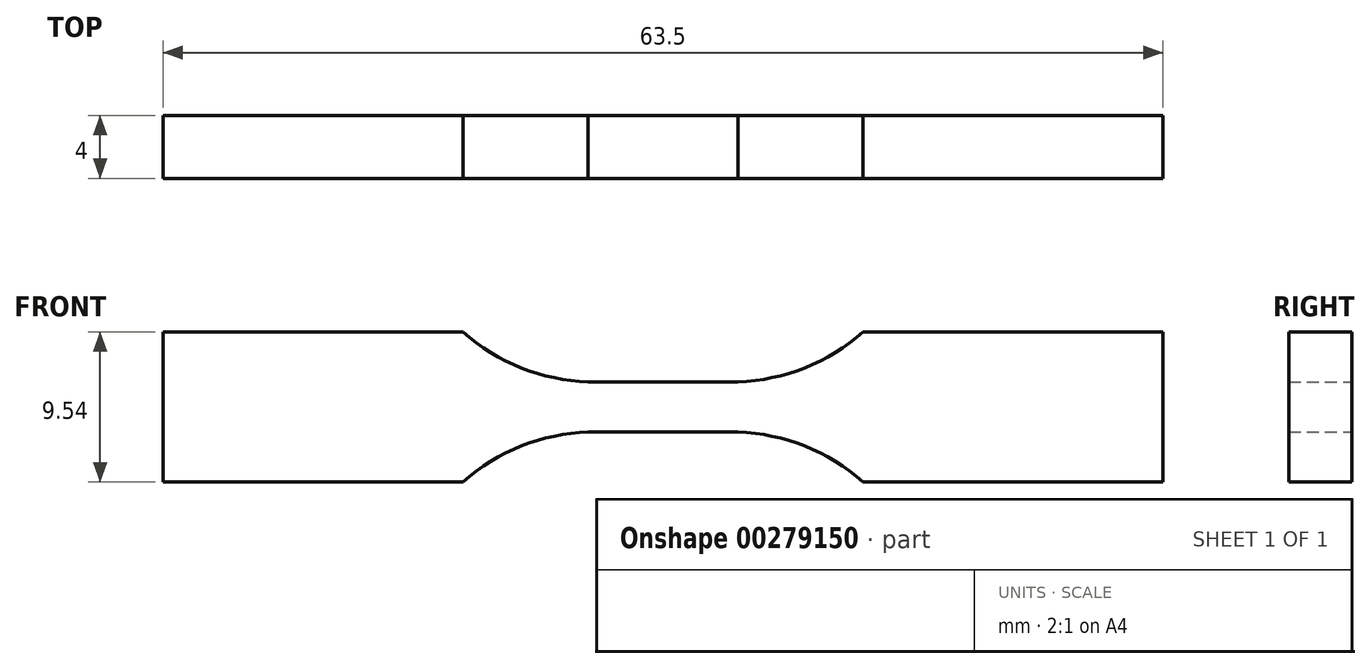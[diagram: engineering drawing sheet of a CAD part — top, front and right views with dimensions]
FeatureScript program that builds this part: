
annotation { "Feature Type Name" : "Feature", "Feature Type Description" : "" }
export const myFeature = defineFeature(function(context is Context, id is Id, definition is map)
    precondition{}
    {
        {
            var Q0;
            Q0=qCreatedBy(makeId("Front.planeOp"),FACE);
            var sketch = newSketch(context, id + "F0", { "sketchPlane" : qUnion([Q0])});
            skLineSegment(sketch, "E0", {"start": v(0, 1.59) * mm, "end": v(4.77, 1.59) * mm});
            skArc(sketch, "E1", {"start": v(4.76, 1.59) * mm, "mid": v(9, 2.49) * mm, "end": v(12.7, 4.76) * mm});
            skLineSegment(sketch, "E2", {"start": v(12.7, 4.77) * mm, "end": v(31.75, 4.77) * mm});
            skLineSegment(sketch, "E3.MirrorCS", {"start": v(12.7, -4.76) * mm, "end": v(31.75, -4.76) * mm});
            skLineSegment(sketch, "E4.MirrorCS", {"start": v(0, -1.59) * mm, "end": v(4.77, -1.59) * mm});
            skArc(sketch, "E5.MirrorCS", {"start": v(4.76, -1.59) * mm, "mid": v(9, -2.49) * mm, "end": v(12.7, -4.76) * mm});
            skArc(sketch, "E6.MirrorCS", {"start": v(-4.76, -1.59) * mm, "mid": v(-9, -2.49) * mm, "end": v(-12.7, -4.76) * mm});
            skLineSegment(sketch, "E7.MirrorCS", {"start": v(0, 1.59) * mm, "end": v(-4.77, 1.59) * mm});
            skArc(sketch, "E8.MirrorCS", {"start": v(-4.76, 1.59) * mm, "mid": v(-9, 2.49) * mm, "end": v(-12.7, 4.76) * mm});
            skLineSegment(sketch, "E9.MirrorCS", {"start": v(-12.7, 4.77) * mm, "end": v(-31.75, 4.77) * mm});
            skLineSegment(sketch, "E10.MirrorCS", {"start": v(-12.7, -4.77) * mm, "end": v(-31.75, -4.77) * mm});
            skLineSegment(sketch, "E11.MirrorCS", {"start": v(0, -1.6) * mm, "end": v(-4.77, -1.6) * mm});
            skLineSegment(sketch, "E12", {"start": v(31.75, 4.77) * mm, "end": v(31.75, -4.77) * mm});
            skLineSegment(sketch, "E13", {"start": v(-31.75, 4.77) * mm, "end": v(-31.75, -4.77) * mm});
            skSolve(sketch);
        }
        {
            var Q0;
            Q0=makeQuery(id+"F0.imprint","IMPRINT",FACE,{"disambiguationData":[TD([[makeQuery(id+"F0.imprint","IMPRINT",EDGE,{"derivedFrom":sQuery(id+"F0.wireOp",EDGE,"E0")}),-1.0]])]});
            extrude(context, id + "F1", {"entities" : qUnion([Q0]), "endBound" : BoundingType.SYMMETRIC, "depth" : 4 * mm});
        }
    });
